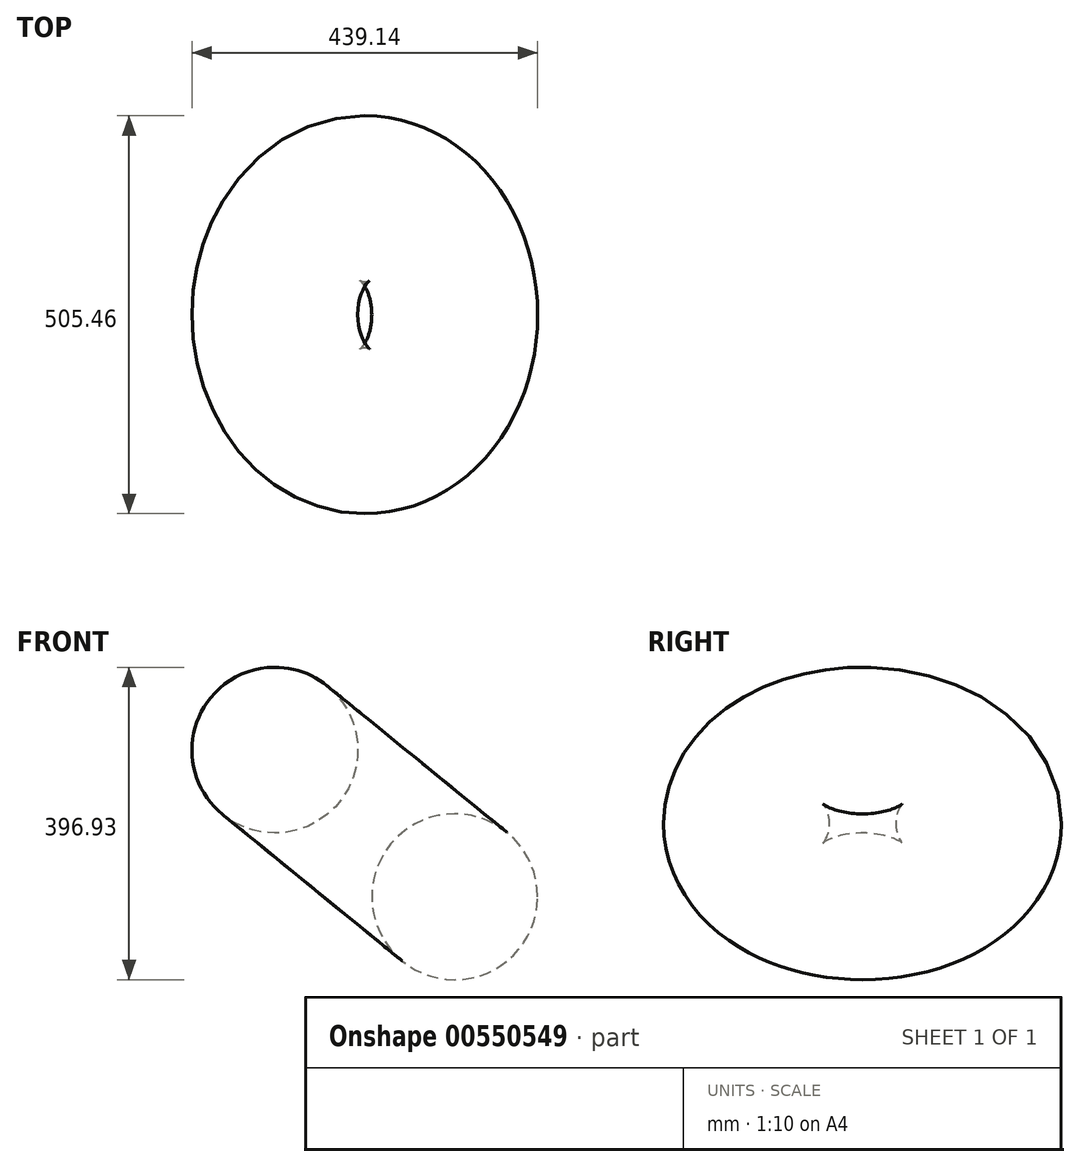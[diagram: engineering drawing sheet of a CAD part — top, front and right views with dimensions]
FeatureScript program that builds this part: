
annotation { "Feature Type Name" : "Feature", "Feature Type Description" : "" }
export const myFeature = defineFeature(function(context is Context, id is Id, definition is map)
    precondition{}
    {
        {
            var Q0;
            Q0=qCreatedBy(makeId("Front.planeOp"),FACE);
            var sketch = newSketch(context, id + "F0", { "sketchPlane" : qUnion([Q0])});
            skCircle(sketch, "E0", {"center": v(0, 0) * mm, "radius": 105.32 * mm});
            skLineSegment(sketch, "E1", {"start": v(190.2, 0) * mm, "end": v(0, -233.28) * mm});
            skSolve(sketch);
        }
        {
            var Q0;
            Q0=makeQuery(id+"F0.imprint","IMPRINT",FACE,{"disambiguationData":[TD([[makeQuery(id+"F0.imprint","IMPRINT",EDGE,{"derivedFrom":sQuery(id+"F0.wireOp",EDGE,"E0")}),1.0]])]});
            var Q1;
            Q1=sQuery(id+"F0.wireOp",EDGE,"E1");
            revolve(context, id + "F1", {"entities" : qUnion([Q0]), "axis" : qUnion([Q1]), "revolveType" : RevolveType.FULL});
        }
    });
